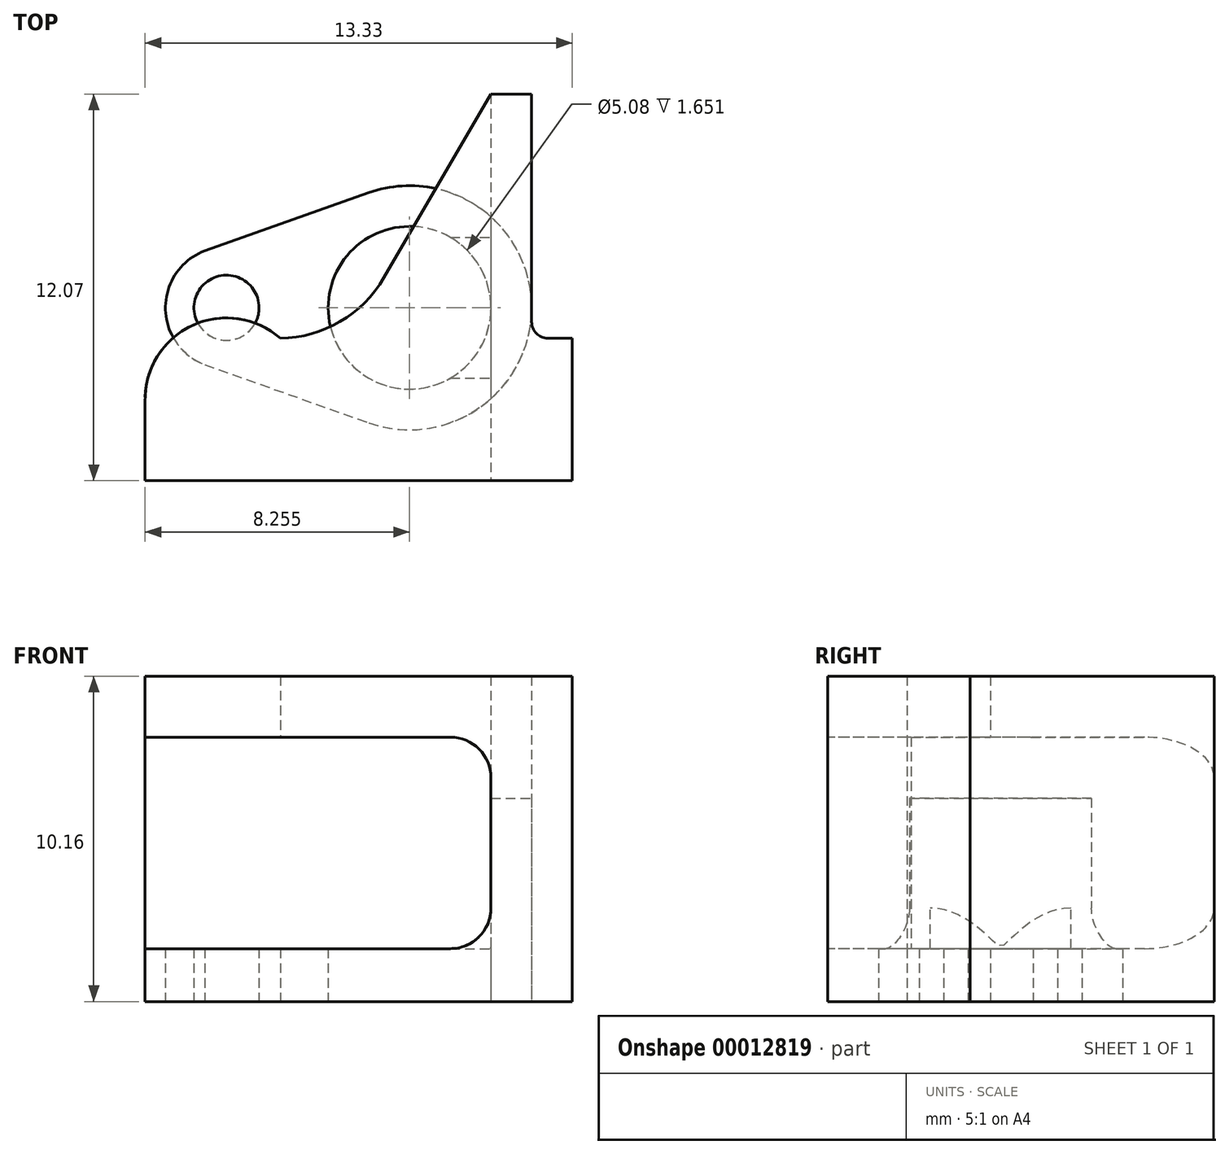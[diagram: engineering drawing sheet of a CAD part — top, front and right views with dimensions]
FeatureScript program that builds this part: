
annotation { "Feature Type Name" : "Feature", "Feature Type Description" : "" }
export const myFeature = defineFeature(function(context is Context, id is Id, definition is map)
    precondition{}
    {
        {
            var Q0;
            Q0=qCreatedBy(makeId("Top.planeOp"),FACE);
            var sketch = newSketch(context, id + "F0", { "sketchPlane" : qUnion([Q0])});
            skPoint(sketch, "E0.start.orphan", {"position": v(0, 4.76) * mm});
            skPoint(sketch, "E1.start.orphan", {"position": v(0, -4.76) * mm});
            skLineSegment(sketch, "E2", {"start": v(9.53, -0.95) * mm, "end": v(9.53, 0) * mm});
            skLineSegment(sketch, "E3.0.MirrorCS", {"start": v(9.53, 6.67) * mm, "end": v(9.53, 0) * mm});
            skLineSegment(sketch, "E4", {"start": v(10.8, -4.76) * mm, "end": v(10.8, -0.95) * mm});
            skLineSegment(sketch, "E5", {"start": v(10.8, -0.95) * mm, "end": v(9.53, -0.95) * mm});
            skPoint(sketch, "E6.end.orphan", {"position": v(8.9, 7.05) * mm});
            skLineSegment(sketch, "E7", {"start": v(9.53, 6.67) * mm, "end": v(8.25, 6.67) * mm});
            skPoint(sketch, "E8.orphan", {"position": v(10.16, 7.81) * mm});
            skLineSegment(sketch, "E9", {"start": v(1.68, -0.95) * mm, "end": v(3.8, -0.95) * mm});
            skPoint(sketch, "E10.start.orphan", {"position": v(10.16, 5.9) * mm});
            skPoint(sketch, "E11.start.orphan", {"position": v(10.16, 2.73) * mm});
            skPoint(sketch, "E12.orphan", {"position": v(0, 2.73) * mm});
            skPoint(sketch, "E13.start.orphan", {"position": v(0, 5.9) * mm});
            skLineSegment(sketch, "E14", {"start": v(8.25, 6.67) * mm, "end": v(3.8, -0.95) * mm});
            skCircle(sketch, "E15", {"center": v(0, -2.86) * mm, "radius": 1.02 * mm});
            skArc(sketch, "E16", {"start": v(1.68, -0.95) * mm, "mid": v(-1.08, -0.56) * mm, "end": v(-2.54, -2.93) * mm});
            skLineSegment(sketch, "E17", {"start": v(-2.54, -5.4) * mm, "end": v(10.8, -5.4) * mm});
            skLineSegment(sketch, "E18", {"start": v(10.8, -5.4) * mm, "end": v(10.8, -4.76) * mm});
            skLineSegment(sketch, "E19", {"start": v(-2.54, -2.93) * mm, "end": v(-2.54, -5.4) * mm});
            skPoint(sketch, "E20.orphan", {"position": v(0, -5.4) * mm});
            skPoint(sketch, "E21.start.orphan", {"position": v(0, -0.95) * mm});
            skPoint(sketch, "E22.orphan", {"position": v(-2.54, -4.76) * mm});
            skPoint(sketch, "E23.end.orphan", {"position": v(9.53, -4.76) * mm});
            skPoint(sketch, "E23.start.orphan", {"position": v(8.26, -4.76) * mm});
            skSolve(sketch);
        }
        {
            var Q0;
            Q0=qSketchRegion(id+"F0",true);
            var Q1;
            Q1=makeQuery(id+"F0.imprint","IMPRINT",FACE,{"disambiguationData":[TD([[makeQuery(id+"F0.imprint","IMPRINT",EDGE,{"derivedFrom":sQuery(id+"F0.wireOp",EDGE,"E15")}),1.0]])]});
            extrude(context, id + "F1", {"entities" : qUnion([Q0, Q1]), "depth" : 10.16 * mm});
        }
        {
            var Q0;
            Q0=qCreatedBy(makeId("Top.planeOp"),FACE);
            var sketch = newSketch(context, id + "F2", { "sketchPlane" : qUnion([Q0])});
            skCircle(sketch, "E24", {"center": v(0, 0) * mm, "radius": 1.02 * mm});
            skArc(sketch, "E25", {"start": v(4.44, -3.6) * mm, "mid": v(9.52, 0) * mm, "end": v(4.44, 3.6) * mm});
            skCircle(sketch, "E26", {"center": v(5.71, 0) * mm, "radius": 2.54 * mm});
            skArc(sketch, "E27", {"start": v(-0.59, 1.81) * mm, "mid": v(-1.9, 0) * mm, "end": v(-0.59, -1.81) * mm});
            skLineSegment(sketch, "E28", {"start": v(-0.68, 1.78) * mm, "end": v(4.44, 3.6) * mm});
            skLineSegment(sketch, "E29.0.MirrorCS", {"start": v(-0.68, -1.78) * mm, "end": v(4.44, -3.6) * mm});
            skSolve(sketch);
        }
        {
            var Q0;
            Q0=makeQuery(id+"F2.imprint","IMPRINT",FACE,{"disambiguationData":[TD([[makeQuery(id+"F2.imprint","IMPRINT",EDGE,{"derivedFrom":sQuery(id+"F2.wireOp",EDGE,"E24")}),-1.0]])]});
            extrude(context, id + "F3", {"entities" : qUnion([Q0]), "depth" : 6.35 * mm});
        }
        {
            var Q0;
            Q0=makeQuery(id+"F1.opExtrude","SWEPT_EDGE",EDGE,{"disambiguationData":[OSD([sQuery(id+"F0.wireOp",EDGE,"E9"),sQuery(id+"F0.wireOp",EDGE,"E14")])]});
            var Q1;
            Q1=makeQuery(id+"F1.opExtrude","SWEPT_EDGE",EDGE,{"disambiguationData":[OSD([sQuery(id+"F0.wireOp",EDGE,"E9"),sQuery(id+"F0.wireOp",EDGE,"E14")])]});
            fillet(context, id + "F4", {"entities" : qUnion([Q0, Q1]), "radius" : 3.8 * mm, "tangentPropagation" : true, "allowEdgeOverflow" : false});
        }
        {
            var Q0;
            Q0=makeQuery(id+"F1.opExtrude","SWEPT_EDGE",EDGE,{"disambiguationData":[OSD([sQuery(id+"F0.wireOp",EDGE,"E2"),sQuery(id+"F0.wireOp",EDGE,"E5")])]});
            fillet(context, id + "F5", {"entities" : qUnion([Q0]), "radius" : 0.5 * mm, "tangentPropagation" : true, "allowEdgeOverflow" : false});
        }
        {
            var Q0;
            Q0=makeQuery(id+"F1.opExtrude","SWEPT_FACE",FACE,{"disambiguationData":[OSD([sQuery(id+"F0.wireOp",EDGE,"E17")])]});
            var sketch = newSketch(context, id + "F6", { "sketchPlane" : qUnion([Q0])});
            skLineSegment(sketch, "E30", {"start": v(-2.54, 8.26) * mm, "end": v(8.26, 8.26) * mm});
            skLineSegment(sketch, "E31", {"start": v(8.26, 8.26) * mm, "end": v(8.26, 1.65) * mm});
            skLineSegment(sketch, "E32", {"start": v(8.26, 1.65) * mm, "end": v(-2.54, 1.65) * mm});
            skSolve(sketch);
        }
        {
            var Q0;
            {var subQ2=sQuery(id+"F6.wireOp",EDGE,"E30");Q0=makeQuery(id+"F6.imprint","IMPRINT",FACE,{"disambiguationData":[TD([[makeQuery(id+"F6.imprint","IMPRINT",EDGE,{"derivedFrom":subQ2}),-1.0]])]});}
            extrude(context, id + "F7", {"entities" : qUnion([Q0]), "operationType" : NewBodyOperationType.REMOVE, "endBound" : BoundingType.THROUGH_ALL, "oppositeDirection" : true, "depth" : 25.4 * mm});
        }
        {
            var Q0;
            Q0=makeQuery(id+"F7.boolean.opBoolean","COPY",EDGE,{"derivedFrom":makeQuery(id+"F7.opExtrude","SWEPT_EDGE",EDGE,{"disambiguationData":[OSD([sQuery(id+"F6.wireOp",EDGE,"E30"),sQuery(id+"F6.wireOp",EDGE,"E31")])]})});
            var Q1;
            Q1=makeQuery(id+"F7.boolean.opBoolean","COPY",EDGE,{"derivedFrom":makeQuery(id+"F7.opExtrude","SWEPT_EDGE",EDGE,{"disambiguationData":[OSD([sQuery(id+"F6.wireOp",EDGE,"E31"),sQuery(id+"F6.wireOp",EDGE,"E32")])]})});
            var Q2;
            {var subQ0=sQuery(id+"F0.wireOp",EDGE,"E9");var subQ1=sQuery(id+"F0.wireOp",EDGE,"E16");Q2=makeQuery(id+"F7.boolean.opBoolean","SPLIT",EDGE,{"disambiguationData":[TD([makeQuery(id+"F7.opExtrude","SWEPT_FACE",FACE,{"disambiguationData":[OSD([sQuery(id+"F6.wireOp",EDGE,"E30")])]})])],"derivedFrom":makeQuery(id+"F1.opExtrude","SWEPT_EDGE",EDGE,{"disambiguationData":[OSD([subQ0,subQ1])]})});}
            var Q3;
            {var subQ0=sQuery(id+"F0.wireOp",EDGE,"E9");var subQ1=sQuery(id+"F0.wireOp",EDGE,"E16");Q3=makeQuery(id+"F7.boolean.opBoolean","SPLIT",EDGE,{"disambiguationData":[TD([makeQuery(id+"F7.opExtrude","SWEPT_FACE",FACE,{"disambiguationData":[OSD([sQuery(id+"F6.wireOp",EDGE,"E32")])]})])],"derivedFrom":makeQuery(id+"F1.opExtrude","SWEPT_EDGE",EDGE,{"disambiguationData":[OSD([subQ0,subQ1])]})});}
            fillet(context, id + "F8", {"entities" : qUnion([Q0, Q1, Q2, Q3]), "radius" : 1.27 * mm, "tangentPropagation" : true, "allowEdgeOverflow" : false});
        }
    });
